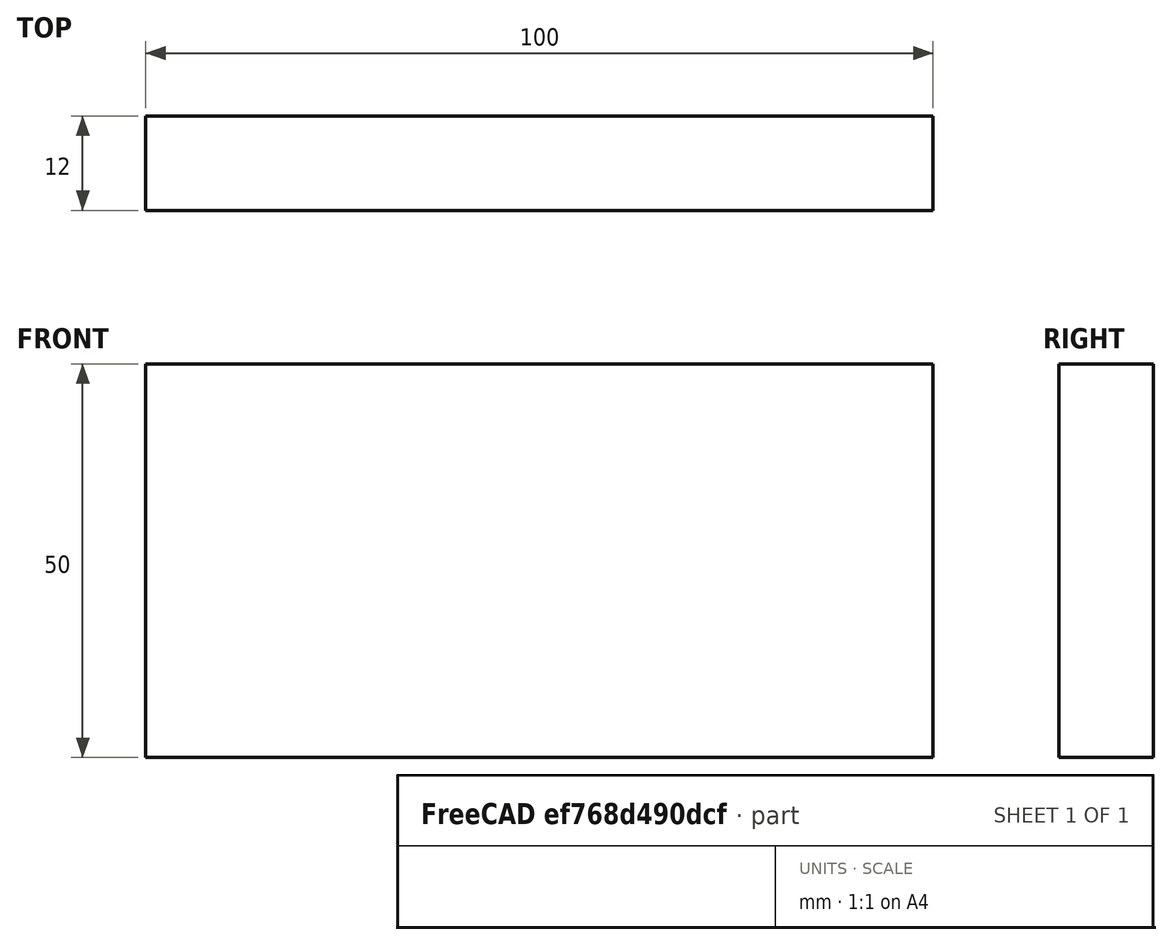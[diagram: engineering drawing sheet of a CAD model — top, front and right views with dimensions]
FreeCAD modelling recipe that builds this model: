
FCSTD DOCUMENT  (FreeCAD 0.15R4671 (Git))
Label: Flat Bar 100x12 EN10058 S235JR
License: All rights reserved
LicenseURL: http://en.wikipedia.org/wiki/All_rights_reserved
objects: Sketcher::SketchObject×1, Part::Extrusion×1
note: 2 computed .brp shape members not serialized (recipe doc carries the construction recipe); baked Part::Feature solids carry a one-line shape summary decoded from their .brp

FEATURE [Sketcher::SketchObject] Sketch
  sketch-geometry (4):
    g0: LineSegment StartX=-50 StartY=-6 StartZ=0 EndX=50 EndY=-6 EndZ=0
    g1: LineSegment StartX=50 StartY=-6 StartZ=0 EndX=50 EndY=6 EndZ=0
    g2: LineSegment StartX=50 StartY=6 StartZ=0 EndX=-50 EndY=6 EndZ=0
    g3: LineSegment StartX=-50 StartY=6 StartZ=0 EndX=-50 EndY=-6 EndZ=0
  constraints (12):
    c: Coincident(g0,g1)
    c: Coincident(g1,g2)
    c: Coincident(g2,g3)
    c: Coincident(g3,g0)
    c: Horizontal(g0)
    c: Horizontal(g2)
    c: Vertical(g1)
    c: Vertical(g3)
    c: Symmetric(g1,g2,g-2)
    c: Symmetric(g0,g1,g-1)
    c: DistanceY(g1) = 12
    c: DistanceX(g0) = 100
FEATURE [Part::Extrusion] Extrude  label="Flat Bar 100x12 EN10058 S235JR"
  Base = -> Sketch
  Dir = (0,0,50)
  Solid = true
